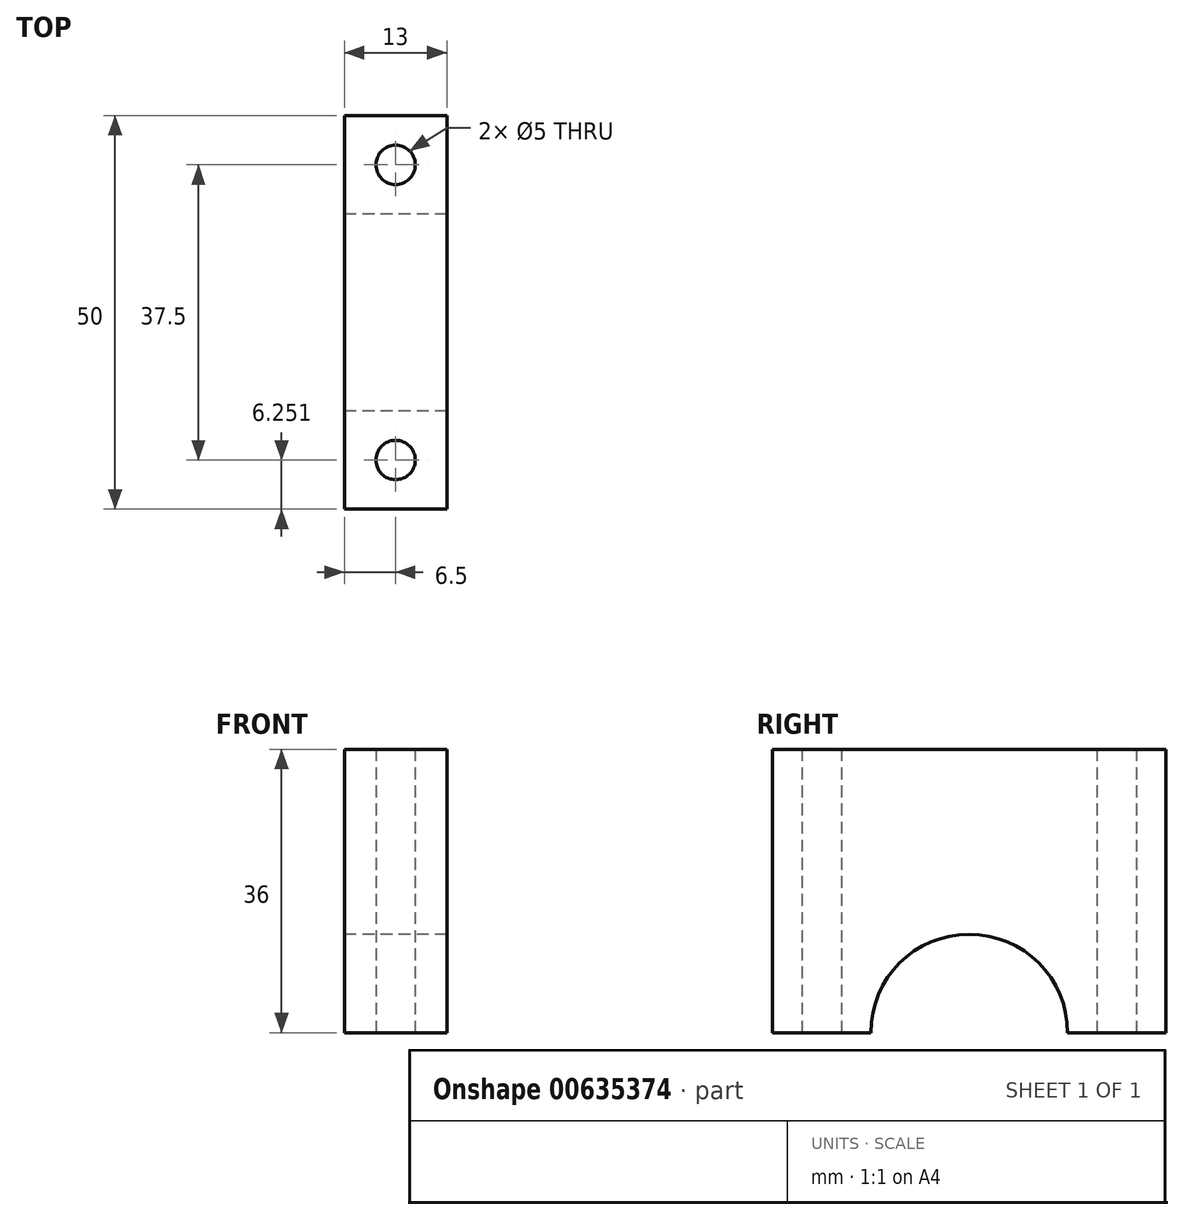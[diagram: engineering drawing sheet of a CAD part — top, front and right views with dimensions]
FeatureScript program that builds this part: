
annotation { "Feature Type Name" : "Feature", "Feature Type Description" : "" }
export const myFeature = defineFeature(function(context is Context, id is Id, definition is map)
    precondition{}
    {
        {
            var Q0;
            Q0=qCreatedBy(makeId("Right.planeOp"),FACE);
            var sketch = newSketch(context, id + "F0", { "sketchPlane" : qUnion([Q0])});
            skLineSegment(sketch, "E0.bottom", {"start": v(-46.65, 17.02) * mm, "end": v(3.35, 17.02) * mm});
            skLineSegment(sketch, "E0.top", {"start": v(-46.65, -18.98) * mm, "end": v(-34.15, -18.98) * mm});
            skLineSegment(sketch, "E0.left", {"start": v(-46.65, 17.02) * mm, "end": v(-46.65, -18.98) * mm});
            skLineSegment(sketch, "E0.right", {"start": v(3.35, 17.02) * mm, "end": v(3.35, -18.98) * mm});
            skArc(sketch, "E1", {"start": v(-9.15, -18.98) * mm, "mid": v(-21.65, -6.48) * mm, "end": v(-34.15, -18.98) * mm});
            skLineSegment(sketch, "E2.trimOffspring", {"start": v(-9.15, -18.98) * mm, "end": v(3.35, -18.98) * mm});
            skSolve(sketch);
        }
        {
            var Q0;
            Q0 = qSketchRegion(id + "F0", true);
            extrude(context, id + "F1", {"entities" : qUnion([Q0]), "depth" : 13 * mm, "offsetDistance" : 25 * mm});
        }
        {
            var Q0;
            Q0=makeQuery(id+"F1.opExtrude","SWEPT_FACE",FACE,{"disambiguationData":[OSD([sQuery(id+"F0.wireOp",EDGE,"E0.top")])]});
            var sketch = newSketch(context, id + "F2", { "sketchPlane" : qUnion([Q0])});
            skCircle(sketch, "E3", {"center": v(6.5, 40.4) * mm, "radius": 2.5 * mm});
            skPoint(sketch, "E3.centerSnap0", {"position": v(13, 40.4) * mm});
            skPoint(sketch, "E3.centerSnap1", {"position": v(6.5, 46.65) * mm});
            skSolve(sketch);
        }
        {
            var Q0;
            Q0=makeQuery(id+"F1.opExtrude","SWEPT_FACE",FACE,{"disambiguationData":[OSD([sQuery(id+"F0.wireOp",EDGE,"E2.trimOffspring")])]});
            var sketch = newSketch(context, id + "F3", { "sketchPlane" : qUnion([Q0])});
            skCircle(sketch, "E4", {"center": v(6.5, 2.9) * mm, "radius": 2.5 * mm});
            skPoint(sketch, "E4.centerSnap0", {"position": v(13, 2.9) * mm});
            skPoint(sketch, "E4.centerSnap1", {"position": v(6.5, 9.15) * mm});
            skSolve(sketch);
        }
        {
            var Q0;
            Q0=makeQuery(id+"F2.imprint","IMPRINT",FACE,{"disambiguationData":[TD([[makeQuery(id+"F2.imprint","IMPRINT",EDGE,{"derivedFrom":sQuery(id+"F2.wireOp",EDGE,"E3")}),1.0]])]});
            extrude(context, id + "F4", {"entities" : qUnion([Q0]), "operationType" : NewBodyOperationType.REMOVE, "oppositeDirection" : true, "depth" : 36 * mm, "offsetDistance" : 25 * mm});
        }
        {
            var Q0;
            Q0=makeQuery(id+"F3.imprint","IMPRINT",FACE,{"disambiguationData":[TD([[makeQuery(id+"F3.imprint","IMPRINT",EDGE,{"derivedFrom":sQuery(id+"F3.wireOp",EDGE,"E4")}),1.0]])]});
            extrude(context, id + "F5", {"entities" : qUnion([Q0]), "operationType" : NewBodyOperationType.REMOVE, "oppositeDirection" : true, "depth" : 36 * mm, "offsetDistance" : 25 * mm});
        }
    });
